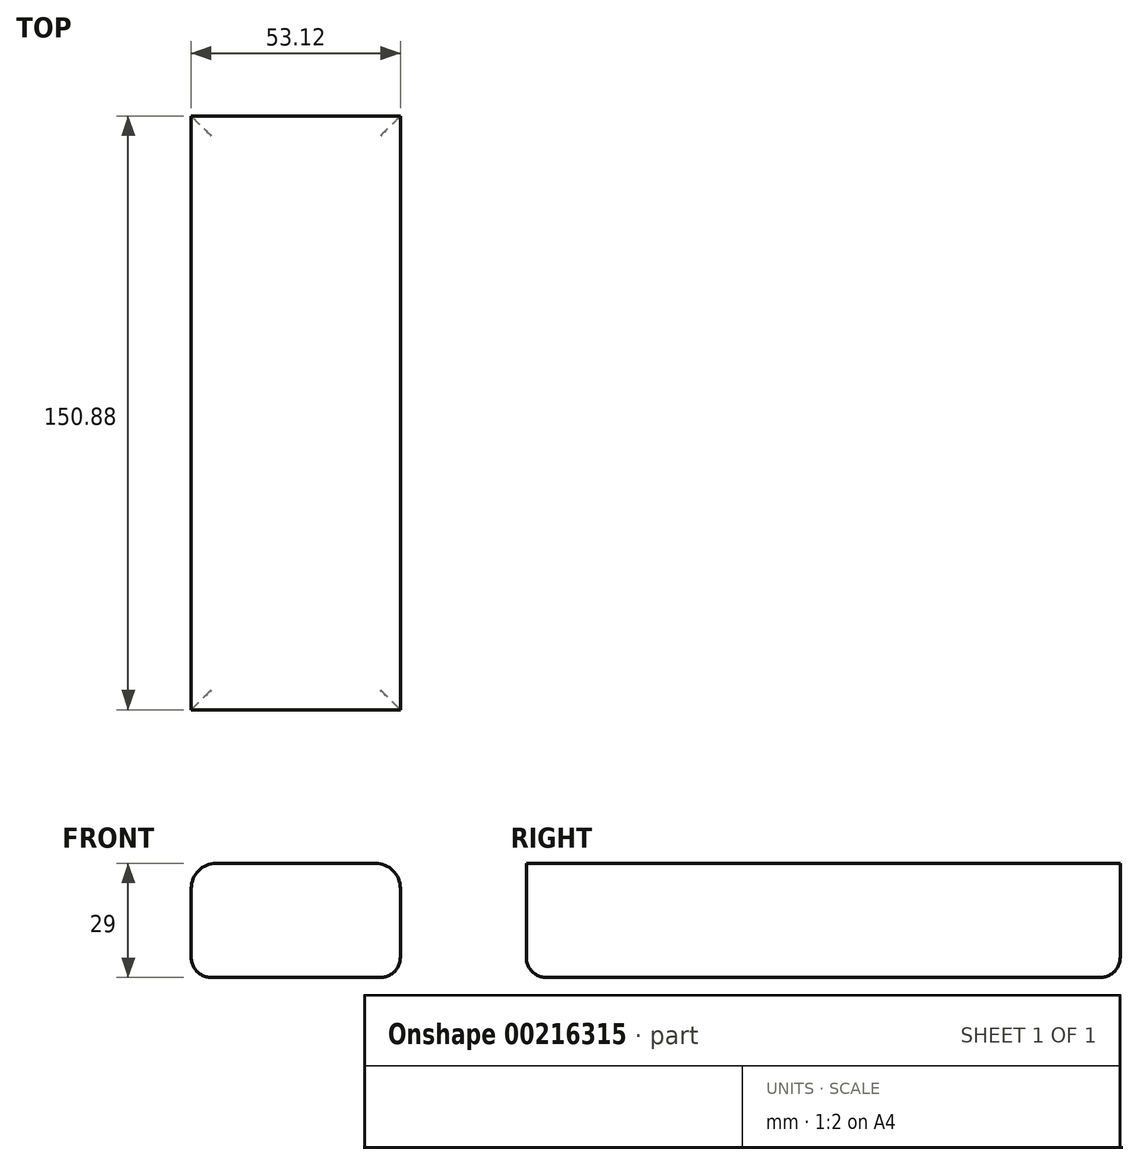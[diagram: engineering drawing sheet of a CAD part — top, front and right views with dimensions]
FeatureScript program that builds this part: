
annotation { "Feature Type Name" : "Feature", "Feature Type Description" : "" }
export const myFeature = defineFeature(function(context is Context, id is Id, definition is map)
    precondition{}
    {
        {
            var Q0;
            Q0=qCreatedBy(makeId("Front.planeOp"),FACE);
            var sketch = newSketch(context, id + "F0", { "sketchPlane" : qUnion([Q0])});
            skLineSegment(sketch, "E0.bottom", {"start": v(0, 0) * mm, "end": v(53.12, 0) * mm});
            skLineSegment(sketch, "E0.top", {"start": v(6.35, 29) * mm, "end": v(46.77, 29) * mm});
            skLineSegment(sketch, "E0.left", {"start": v(0, 0) * mm, "end": v(0, 22.65) * mm});
            skLineSegment(sketch, "E0.right", {"start": v(53.12, 0) * mm, "end": v(53.12, 22.65) * mm});
            skPoint(sketch, "E1.visualSharp", {"position": v(0, 29) * mm});
            skArc(sketch, "E1.filletArc", {"start": v(6.35, 29) * mm, "mid": v(1.86, 27.14) * mm, "end": v(0, 22.65) * mm});
            skPoint(sketch, "E2.visualSharp", {"position": v(53.12, 29) * mm});
            skArc(sketch, "E2.filletArc", {"start": v(53.12, 22.65) * mm, "mid": v(51.26, 27.14) * mm, "end": v(46.77, 29) * mm});
            skSolve(sketch);
        }
        {
            var Q0;
            Q0=makeQuery(id+"F0.imprint","IMPRINT",FACE,{"disambiguationData":[TD([[makeQuery(id+"F0.imprint","IMPRINT",EDGE,{"derivedFrom":sQuery(id+"F0.wireOp",EDGE,"E0.bottom")}),1.0]])]});
            extrude(context, id + "F1", {"entities" : qUnion([Q0]), "depth" : 150.88 * mm});
        }
        {
            var Q0;
            Q0=makeQuery(id+"F1.opExtrude","SWEPT_EDGE",EDGE,{"disambiguationData":[OSD([sQuery(id+"F0.wireOp",EDGE,"E0.bottom"),sQuery(id+"F0.wireOp",EDGE,"E0.right")])]});
            var Q1;
            Q1=makeQuery(id+"F1.opExtrude","CAP_EDGE",EDGE,{"disambiguationData":[OSD([sQuery(id+"F0.wireOp",EDGE,"E0.bottom")])],"isStart":false});
            var Q2;
            Q2=makeQuery(id+"F1.opExtrude","SWEPT_EDGE",EDGE,{"disambiguationData":[OSD([sQuery(id+"F0.wireOp",EDGE,"E0.bottom"),sQuery(id+"F0.wireOp",EDGE,"E0.left")])]});
            var Q3;
            Q3=makeQuery(id+"F1.opExtrude","CAP_EDGE",EDGE,{"disambiguationData":[OSD([sQuery(id+"F0.wireOp",EDGE,"E0.bottom")])],"isStart":true});
            fillet(context, id + "F2", {"entities" : qUnion([Q0, Q1, Q2, Q3]), "radius" : 5.08 * mm, "tangentPropagation" : true, "allowEdgeOverflow" : false});
        }
    });
